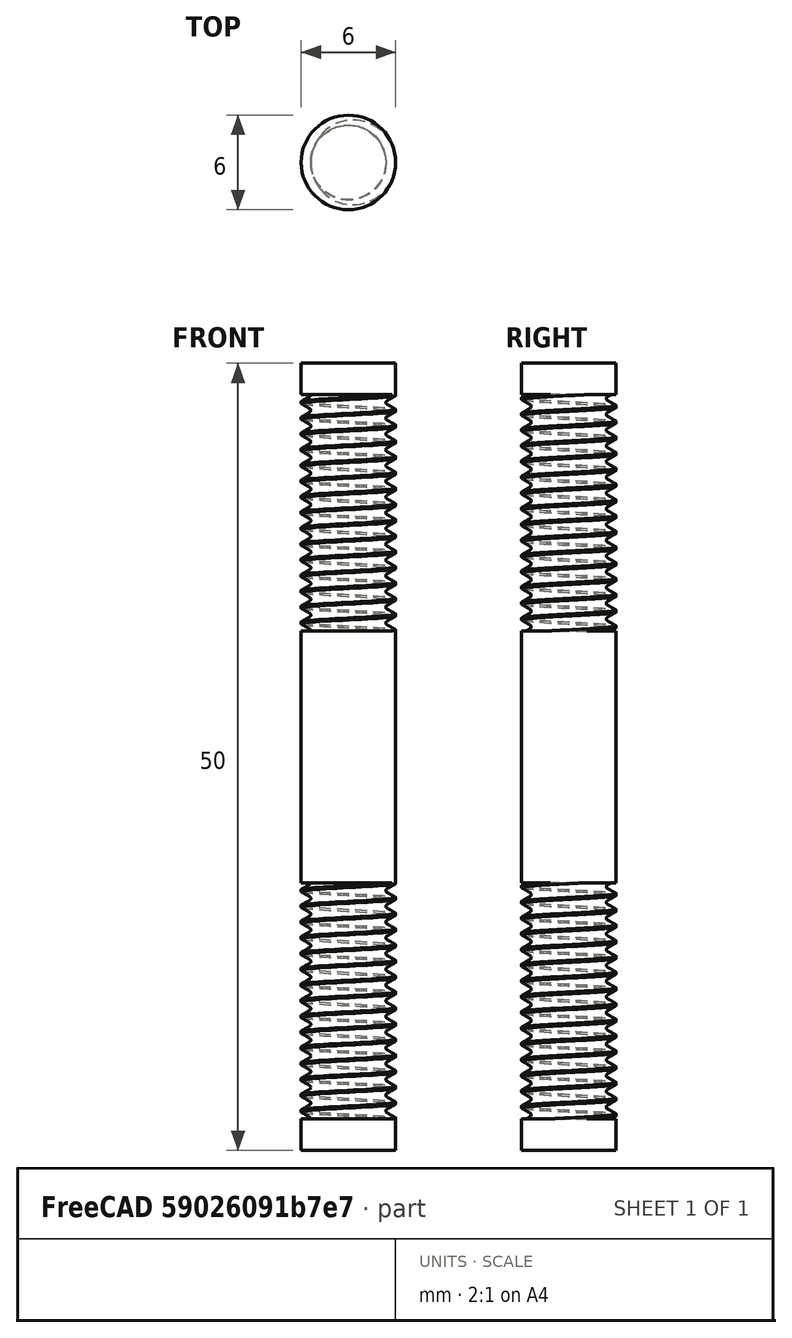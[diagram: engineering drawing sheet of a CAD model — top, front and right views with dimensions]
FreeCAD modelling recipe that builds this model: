
FCSTD DOCUMENT  (FreeCAD 1.0R39319 (Git))
Label: Assignment_2_Tension_Rod
License: All rights reserved
LicenseURL: https://en.wikipedia.org/wiki/All_rights_reserved
objects: Part::FeaturePython×2, Part::Cut×2, Sketcher::SketchObject×1, PartDesign::Body×1, PartDesign::Pad×1
note: 10 computed .brp shape members not serialized (recipe doc carries the construction recipe); baked Part::Feature solids carry a one-line shape summary decoded from their .brp

FEATURE [Sketcher::SketchObject] Sketch
  ArcFitTolerance = 1e-06
  AttachmentSupport = -> [XY_Plane]
  FullyConstrained = true
  MakeInternals = false
  MapMode = 5
  sketch-geometry (1):
    g0: Circle CenterX=0 CenterY=0 CenterZ=0 NormalX=0 NormalY=0 NormalZ=1 AngleXU=0 Radius=3
  constraints (2):
    c: Coincident(g0,g-1)
    c: Diameter(g0) = 6
FEATURE [PartDesign::Body] Body
  AllowCompound = false
  Group = -> [Sketch]
  Origin = -> Origin
FEATURE [PartDesign::Pad] Pad
  Direction = (0,0,1)
  Length = 50
  Length2 = 10
  Profile = -> Sketch
  ReferenceAxis = -> Sketch [N_Axis]
  Refine = true
  Suppressed = false
  Type = 0
FEATURE [Part::FeaturePython] ScrewDie  label="M6x15-ScrewDie"  # WARN: FeaturePython — macro-defined, semantics opaque (R4)
  Diameter = 8
  DiameterCustom = 6
  Invert = false
  LeftHanded = false
  Length = 15
  MatchOuter = false
  OffsetAngle = 0
  PitchCustom = 1
  Placement = pos=(0,0,17) rot=(0,0,1;0rad)
  Thread = true
  Type = 0
FEATURE [Part::Cut] Cut
  Base = -> Pad
  Refine = true
  Tool = -> ScrewDie
FEATURE [Part::FeaturePython] ScrewDie001  label="M6x15-ScrewDie001"  # WARN: FeaturePython — macro-defined, semantics opaque (R4)
  Diameter = 8
  DiameterCustom = 6
  Invert = false
  LeftHanded = false
  Length = 15
  MatchOuter = false
  OffsetAngle = 0
  PitchCustom = 1
  Placement = pos=(0,0,48) rot=(0,0,1;0rad)
  Thread = true
  Type = 0
FEATURE [Part::Cut] Cut001
  Base = -> Cut
  Refine = true
  Tool = -> ScrewDie001
